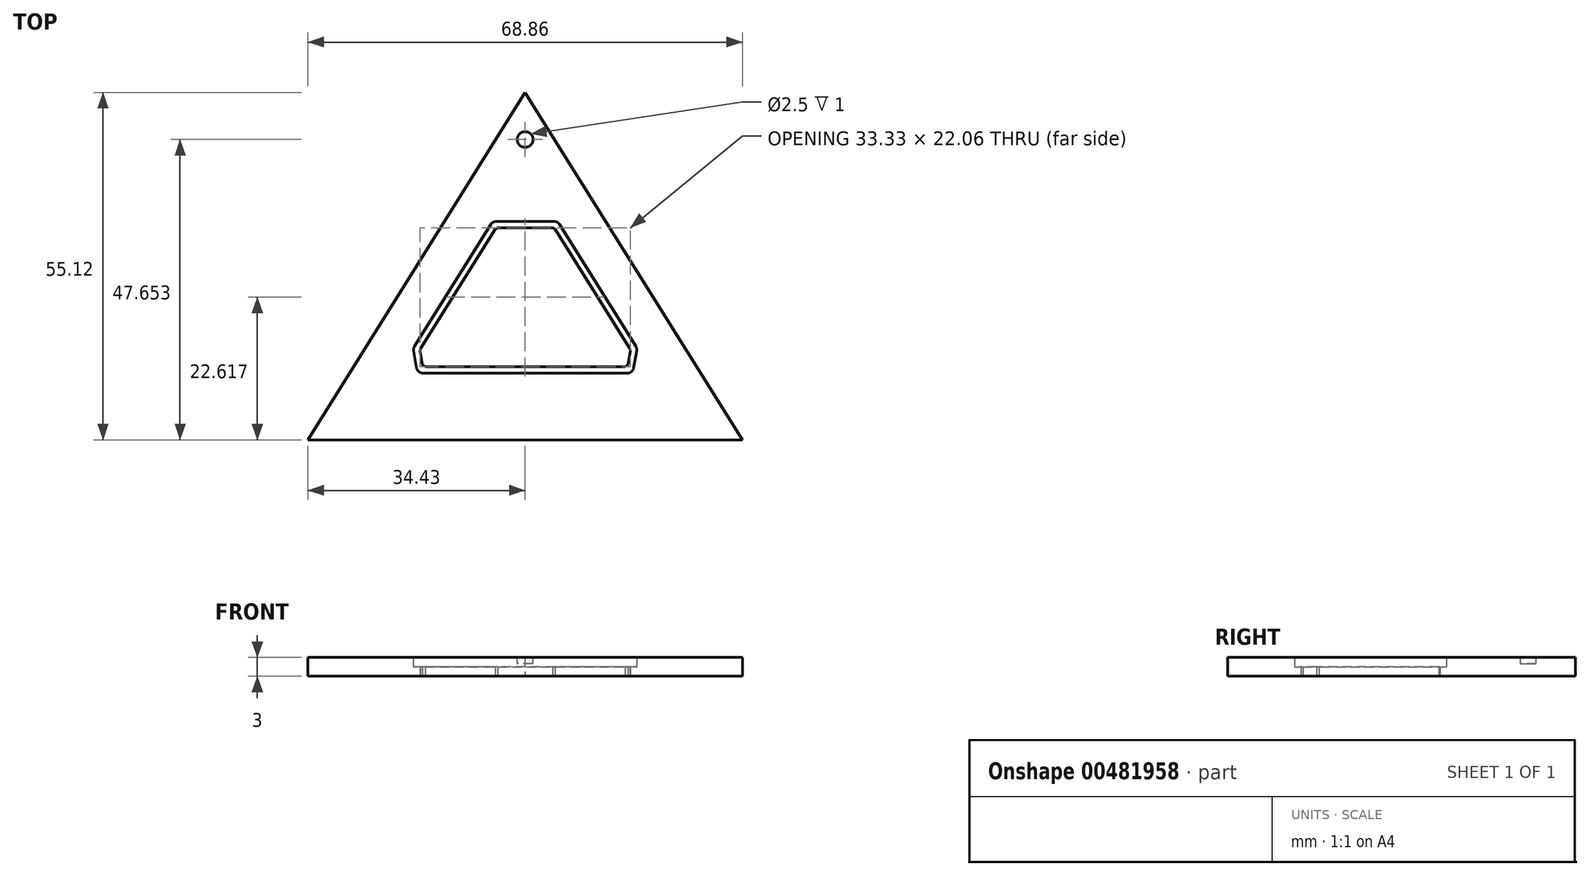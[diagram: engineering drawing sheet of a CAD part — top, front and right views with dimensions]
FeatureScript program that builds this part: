
annotation { "Feature Type Name" : "Feature", "Feature Type Description" : "" }
export const myFeature = defineFeature(function(context is Context, id is Id, definition is map)
    precondition{}
    {
        {
            var Q0;
            Q0=qCreatedBy(makeId("Top.planeOp"),FACE);
            var sketch = newSketch(context, id + "F0", { "sketchPlane" : qUnion([Q0])});
            skLineSegment(sketch, "E0", {"start": v(-34.43, 0) * mm, "end": v(34.43, 0) * mm});
            skLineSegment(sketch, "E1", {"start": v(-34.43, 0) * mm, "end": v(0, 55.13) * mm});
            skLineSegment(sketch, "E2", {"start": v(0, 55.13) * mm, "end": v(34.43, 0) * mm});
            skLineSegment(sketch, "E3.0", {"start": v(5.16, 34.65) * mm, "end": v(17.75, 14.49) * mm});
            skLineSegment(sketch, "E4.trimOffspring", {"start": v(-17.06, 10.59) * mm, "end": v(17.06, 10.59) * mm});
            skLineSegment(sketch, "E5.trimOffspring", {"start": v(-17.75, 14.49) * mm, "end": v(-5.16, 34.65) * mm});
            skLineSegment(sketch, "E6.trimOffspring", {"start": v(-5.16, 34.65) * mm, "end": v(5.16, 34.65) * mm});
            skLineSegment(sketch, "E7", {"start": v(17.06, 10.59) * mm, "end": v(17.75, 14.49) * mm});
            skLineSegment(sketch, "E8.MirrorCS", {"start": v(-17.06, 10.59) * mm, "end": v(-17.75, 14.49) * mm});
            skSolve(sketch);
        }
        {
            var Q0;
            Q0 = qSketchRegion(id + "F0", true);
            extrude(context, id + "F1", {"entities" : qUnion([Q0]), "depth" : 3 * mm});
        }
        {
            var Q0;
            Q0=makeQuery(id+"F1.opExtrude","SWEPT_EDGE",EDGE,{"disambiguationData":[OSD([sQuery(id+"F0.wireOp",EDGE,"E4.trimOffspring"),sQuery(id+"F0.wireOp",EDGE,"E7")])]});
            var Q1;
            Q1=makeQuery(id+"F1.opExtrude","SWEPT_EDGE",EDGE,{"disambiguationData":[OSD([sQuery(id+"F0.wireOp",EDGE,"E4.trimOffspring"),sQuery(id+"F0.wireOp",EDGE,"E8.MirrorCS")])]});
            var Q2;
            Q2=makeQuery(id+"F1.opExtrude","SWEPT_EDGE",EDGE,{"disambiguationData":[OSD([sQuery(id+"F0.wireOp",EDGE,"E3.0"),sQuery(id+"F0.wireOp",EDGE,"E7")])]});
            var Q3;
            Q3=makeQuery(id+"F1.opExtrude","SWEPT_EDGE",EDGE,{"disambiguationData":[OSD([sQuery(id+"F0.wireOp",EDGE,"E5.trimOffspring"),sQuery(id+"F0.wireOp",EDGE,"E8.MirrorCS")])]});
            var Q4;
            Q4=makeQuery(id+"F1.opExtrude","SWEPT_EDGE",EDGE,{"disambiguationData":[OSD([sQuery(id+"F0.wireOp",EDGE,"E3.0"),sQuery(id+"F0.wireOp",EDGE,"E6.trimOffspring")])]});
            var Q5;
            Q5=makeQuery(id+"F1.opExtrude","SWEPT_EDGE",EDGE,{"disambiguationData":[OSD([sQuery(id+"F0.wireOp",EDGE,"E5.trimOffspring"),sQuery(id+"F0.wireOp",EDGE,"E6.trimOffspring")])]});
            fillet(context, id + "F2", {"entities" : qUnion([Q0, Q1, Q2, Q3, Q4, Q5]), "radius" : 1 * mm, "tangentPropagation" : true, "allowEdgeOverflow" : false});
        }
        {
            var Q0;
            Q0=makeQuery(id+"F1.opExtrude","CAP_FACE",FACE,{"disambiguationData":[OSD([sQuery(id+"F0.wireOp",EDGE,"E0"),sQuery(id+"F0.wireOp",EDGE,"E1"),sQuery(id+"F0.wireOp",EDGE,"E2"),sQuery(id+"F0.wireOp",EDGE,"E3.0"),sQuery(id+"F0.wireOp",EDGE,"E4.trimOffspring"),sQuery(id+"F0.wireOp",EDGE,"E5.trimOffspring"),sQuery(id+"F0.wireOp",EDGE,"E6.trimOffspring"),sQuery(id+"F0.wireOp",EDGE,"E7"),sQuery(id+"F0.wireOp",EDGE,"E8.MirrorCS")])],"isStart":false});
            var sketch = newSketch(context, id + "F3", { "sketchPlane" : qUnion([Q0])});
            skCircle(sketch, "E9", {"center": v(0, 47.65) * mm, "radius": 1.25 * mm});
            skPoint(sketch, "E9.centerSnap0", {"position": v(0, 0) * mm});
            skSolve(sketch);
        }
        {
            var Q0;
            Q0 = qSketchRegion(id + "F3", true);
            extrude(context, id + "F4", {"entities" : qUnion([Q0]), "operationType" : NewBodyOperationType.REMOVE, "oppositeDirection" : true, "depth" : 1 * mm});
        }
        {
            var Q0;
            Q0=makeQuery(id+"F1.opExtrude","CAP_FACE",FACE,{"disambiguationData":[OSD([sQuery(id+"F0.wireOp",EDGE,"E0"),sQuery(id+"F0.wireOp",EDGE,"E1"),sQuery(id+"F0.wireOp",EDGE,"E2"),sQuery(id+"F0.wireOp",EDGE,"E3.0"),sQuery(id+"F0.wireOp",EDGE,"E4.trimOffspring"),sQuery(id+"F0.wireOp",EDGE,"E5.trimOffspring"),sQuery(id+"F0.wireOp",EDGE,"E6.trimOffspring"),sQuery(id+"F0.wireOp",EDGE,"E7"),sQuery(id+"F0.wireOp",EDGE,"E8.MirrorCS")])],"isStart":true});
            var sketch = newSketch(context, id + "F5", { "sketchPlane" : qUnion([Q0])});
            skLineSegment(sketch, "E10.0", {"start": v(-4.34, -33.65) * mm, "end": v(-4.74, -33.43) * mm});
            skLineSegment(sketch, "E10.1", {"start": v(16.28, -11.95) * mm, "end": v(16.66, -14.1) * mm});
            skLineSegment(sketch, "E10.2", {"start": v(16.66, -14.1) * mm, "end": v(16.6, -14.44) * mm});
            skLineSegment(sketch, "E10.3", {"start": v(16.6, -14.44) * mm, "end": v(4.74, -33.43) * mm});
            skLineSegment(sketch, "E10.4", {"start": v(4.34, -33.65) * mm, "end": v(4.74, -33.43) * mm});
            skLineSegment(sketch, "E10.5", {"start": v(15.86, -11.59) * mm, "end": v(16.28, -11.95) * mm});
            skLineSegment(sketch, "E10.6", {"start": v(-4.34, -33.65) * mm, "end": v(4.34, -33.65) * mm});
            skLineSegment(sketch, "E10.7", {"start": v(-15.86, -11.59) * mm, "end": v(15.86, -11.59) * mm});
            skLineSegment(sketch, "E10.8", {"start": v(-15.86, -11.59) * mm, "end": v(-16.28, -11.95) * mm});
            skLineSegment(sketch, "E10.9", {"start": v(-16.28, -11.95) * mm, "end": v(-16.66, -14.1) * mm});
            skLineSegment(sketch, "E10.10", {"start": v(-16.6, -14.44) * mm, "end": v(-16.66, -14.1) * mm});
            skLineSegment(sketch, "E10.11", {"start": v(-4.74, -33.43) * mm, "end": v(-16.6, -14.44) * mm});
            skLineSegment(sketch, "E11.0", {"start": v(20.43, -14.13) * mm, "end": v(20.1, -15.82) * mm});
            skLineSegment(sketch, "E11.1", {"start": v(-7.37, -36.2) * mm, "end": v(-20.1, -15.82) * mm});
            skLineSegment(sketch, "E11.2", {"start": v(-5.3, -37.35) * mm, "end": v(-7.37, -36.2) * mm});
            skLineSegment(sketch, "E11.3", {"start": v(-5.3, -37.35) * mm, "end": v(5.3, -37.35) * mm});
            skLineSegment(sketch, "E11.4", {"start": v(5.3, -37.35) * mm, "end": v(7.37, -36.2) * mm});
            skLineSegment(sketch, "E11.5", {"start": v(-20.1, -15.82) * mm, "end": v(-20.43, -14.13) * mm});
            skLineSegment(sketch, "E11.6", {"start": v(20.1, -15.82) * mm, "end": v(7.37, -36.2) * mm});
            skLineSegment(sketch, "E11.7", {"start": v(-19.7, -9.98) * mm, "end": v(-20.43, -14.13) * mm});
            skLineSegment(sketch, "E11.8", {"start": v(-17.2, -7.89) * mm, "end": v(-19.7, -9.98) * mm});
            skLineSegment(sketch, "E11.9", {"start": v(-17.2, -7.89) * mm, "end": v(17.2, -7.89) * mm});
            skLineSegment(sketch, "E11.10", {"start": v(17.2, -7.89) * mm, "end": v(19.7, -9.98) * mm});
            skLineSegment(sketch, "E11.11", {"start": v(19.7, -9.98) * mm, "end": v(20.43, -14.13) * mm});
            skSolve(sketch);
        }
        {
            var Q0;
            Q0 = qSketchRegion(id + "F5", true);
            extrude(context, id + "F6", {"entities" : qUnion([Q0]), "operationType" : NewBodyOperationType.ADD, "oppositeDirection" : true, "depth" : 1.5 * mm});
        }
    });
